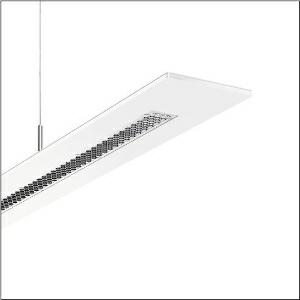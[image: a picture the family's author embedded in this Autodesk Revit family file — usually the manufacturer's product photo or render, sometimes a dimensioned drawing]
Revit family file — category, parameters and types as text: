
# Revit family: arktika_r__21_duo_5mb252dl60830_d82e
name_source: partatom
category: Lighting Fixtures
units: mm (PartAtom-declared; Revit-internal decimal feet)

## family parameters
Cut with Voids When Loaded = No
Host = Face
Light Source = No
Part Type = Normal
Room Calculation Point = No
Round Connector Dimension = Use Diameter
Shared = No

## types (1)
- --- (1 x LED 3000K / CRI = 80 (unbekannt), 8100 lm, 3000K)
    Apparent Load = 67 VA
    CIE Flux Codes = 81 100 100 79 100
    Color Rendering = 80
    Color Temperature = 3000K
    Default Elevation = 1800 mm
    Description = Arktika® 21, office luminaire, primary anti-glare with honeycomb louvre, of plastic, aluminium vaporised, highly specular, light emission: direct/indirect distribution, primary light characteristic: symmetric, installation type: suspended mounting, LED rated luminous flux: 8.100 lm, light colour: 830, colour temperature: 3000K, control gear: ECG DALI, with terminal, 3+2-pole, max. 2.5mm², mains connection: 220..240V, AC, 50/60Hz, rated input power: 67W, housing, of aluminium, powder-coated, traffic white (RAL 9016), 2-length, length: 2.280 mm, width: 120 mm, height: 8mm, protection rating (complete): IP20, insulation class (complete): insulation class II (safety insulation), certification: CE, packaging unit: 1 piece
    Height = 8 mm  [stored 0.0262467 ft]
    Lamp = 1 x LED 3000K / CRI >= 80 (unbekannt)
    Lamp Light Flux = 8100 lm
    Lamp count = 1
    Length = 2280 mm
    Luminous efficacy = 122 lm/W
    Manufacturer = Siteco
    ModVariant = No
    Model = 5MB252DL60830
    Mounting Place = Ceiling
    Mounting Type = Pendant
    Number of Poles = 1
    OnlyDefault = Yes
    Power Factor = 1
    Product Name = Arktika® 21 duo
    Product group = office luminaire | ceiling pendant
    ProductGroupID = 905
    Protection Class = Protection class II
    Protection Degree = IP 20
    RLX_Detail_Level = 1
    RlxData = <blob elided: 39749 chars, md5=256ecacf>
    Socket = socket
    Standby Power = 0 W
    System Light Flux = 8100 lm
    System Power = 67 W
    Type Comments = factory setting: luminous flux: 100 % | dim-lin: 254 | 1330 mA
    Type Image = l_1006128.jpg
    URL = http://relux.com
    VarID = @adj_145833
    Voltage = 0 V
    Weight = 0.00 kg
    Width = 120 mm

note: [stored X ft] marks values corroborated as IEEE doubles in the binary element streams (Revit-internal decimal feet)

## geometry (parser evidence)
native form markers: Blend x4, Sweep x10
no freeform markers — native parametric forms only
